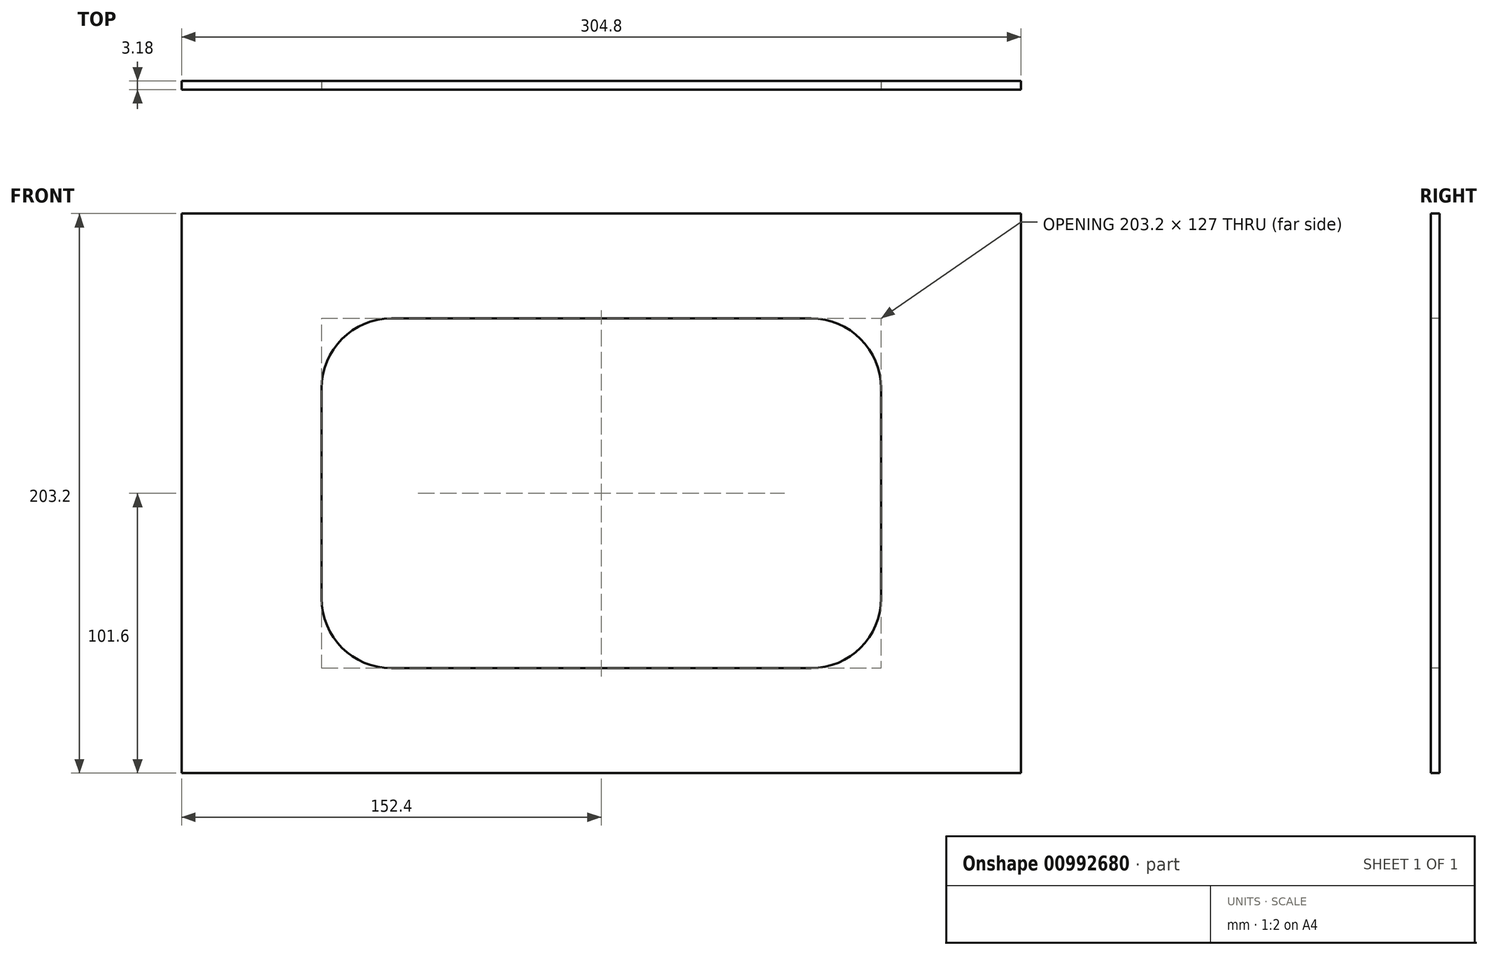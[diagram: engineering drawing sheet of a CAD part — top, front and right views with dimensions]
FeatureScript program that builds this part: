
annotation { "Feature Type Name" : "Feature", "Feature Type Description" : "" }
export const myFeature = defineFeature(function(context is Context, id is Id, definition is map)
    precondition{}
    {
        {
            var Q0;
            Q0=qCreatedBy(makeId("Front.planeOp"),FACE);
            var sketch = newSketch(context, id + "F0", { "sketchPlane" : qUnion([Q0])});
            skLineSegment(sketch, "E0.bottom", {"start": v(152.4, 101.6) * mm, "end": v(-152.4, 101.6) * mm});
            skLineSegment(sketch, "E0.top", {"start": v(152.4, -101.6) * mm, "end": v(-152.4, -101.6) * mm});
            skLineSegment(sketch, "E0.left", {"start": v(152.4, 101.6) * mm, "end": v(152.4, -101.6) * mm});
            skLineSegment(sketch, "E0.right", {"start": v(-152.4, 101.6) * mm, "end": v(-152.4, -101.6) * mm});
            skPoint(sketch, "E0.middle", {"position": v(0, 0) * mm});
            skSolve(sketch);
        }
        {
            var Q0;
            Q0=makeQuery(id+"F0.imprint","IMPRINT",FACE,{"disambiguationData":[TD([[makeQuery(id+"F0.imprint","IMPRINT",EDGE,{"derivedFrom":sQuery(id+"F0.wireOp",EDGE,"E0.bottom")}),1.0]])]});
            extrude(context, id + "F1", {"entities" : qUnion([Q0]), "depth" : 3.17 * mm, "offsetDistance" : 25.4 * mm});
        }
        {
            var Q0;
            Q0=makeQuery(id+"F1.opExtrude","CAP_FACE",FACE,{"disambiguationData":[OSD([sQuery(id+"F0.wireOp",EDGE,"E0.bottom"),sQuery(id+"F0.wireOp",EDGE,"E0.top"),sQuery(id+"F0.wireOp",EDGE,"E0.left"),sQuery(id+"F0.wireOp",EDGE,"E0.right")])],"isStart":false});
            var sketch = newSketch(context, id + "F2", { "sketchPlane" : qUnion([Q0])});
            skLineSegment(sketch, "E1.bottom", {"start": v(101.6, 63.5) * mm, "end": v(-101.6, 63.5) * mm});
            skLineSegment(sketch, "E1.top", {"start": v(101.6, -63.5) * mm, "end": v(-101.6, -63.5) * mm});
            skLineSegment(sketch, "E1.left", {"start": v(101.6, 63.5) * mm, "end": v(101.6, -63.5) * mm});
            skLineSegment(sketch, "E1.right", {"start": v(-101.6, 63.5) * mm, "end": v(-101.6, -63.5) * mm});
            skPoint(sketch, "E1.middle", {"position": v(0, 0) * mm});
            skSolve(sketch);
        }
        {
            var Q0;
            Q0=makeQuery(id+"F2.imprint","IMPRINT",FACE,{"disambiguationData":[TD([[makeQuery(id+"F2.imprint","IMPRINT",EDGE,{"derivedFrom":sQuery(id+"F2.wireOp",EDGE,"E1.bottom")}),1.0]])]});
            extrude(context, id + "F3", {"entities" : qUnion([Q0]), "operationType" : NewBodyOperationType.REMOVE, "oppositeDirection" : true, "depth" : 25.4 * mm, "offsetDistance" : 25.4 * mm});
        }
        {
            var Q0;
            Q0=makeQuery(id+"F3.boolean.opBoolean","COPY",EDGE,{"derivedFrom":makeQuery(id+"F3.opExtrude","SWEPT_EDGE",EDGE,{"disambiguationData":[OSD([sQuery(id+"F2.wireOp",EDGE,"E1.bottom"),sQuery(id+"F2.wireOp",EDGE,"E1.right")])]})});
            var Q1;
            Q1=makeQuery(id+"F3.boolean.opBoolean","COPY",EDGE,{"derivedFrom":makeQuery(id+"F3.opExtrude","SWEPT_EDGE",EDGE,{"disambiguationData":[OSD([sQuery(id+"F2.wireOp",EDGE,"E1.top"),sQuery(id+"F2.wireOp",EDGE,"E1.right")])]})});
            var Q2;
            Q2=makeQuery(id+"F3.boolean.opBoolean","COPY",EDGE,{"derivedFrom":makeQuery(id+"F3.opExtrude","SWEPT_EDGE",EDGE,{"disambiguationData":[OSD([sQuery(id+"F2.wireOp",EDGE,"E1.top"),sQuery(id+"F2.wireOp",EDGE,"E1.left")])]})});
            var Q3;
            Q3=makeQuery(id+"F3.boolean.opBoolean","COPY",EDGE,{"derivedFrom":makeQuery(id+"F3.opExtrude","SWEPT_EDGE",EDGE,{"disambiguationData":[OSD([sQuery(id+"F2.wireOp",EDGE,"E1.bottom"),sQuery(id+"F2.wireOp",EDGE,"E1.left")])]})});
            fillet(context, id + "F4", {"entities" : qUnion([Q0, Q1, Q2, Q3]), "radius" : 25.4 * mm, "tangentPropagation" : true, "allowEdgeOverflow" : false});
        }
    });
